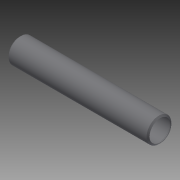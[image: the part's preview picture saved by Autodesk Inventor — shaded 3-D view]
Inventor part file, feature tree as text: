
AUTODESK INVENTOR PART (.ipt)
format: ipt  version: 2014 (Build 180170000, 170)  size: 118,784 bytes
history: native  units: in
note: dims shown in document units (in); Inventor stores cm internally (conversion verified against a paired STEP export)
features: other x56, revolve x1, sketch x1
ambient origin geometry x8: Origin, YZ Plane, XZ Plane, XY Plane, X Axis, Y Axis, Z Axis, Center Point
bodies: Solid1 (feature_tree)
feature tree (58):
  revolve  "Revolution1"  [1 undecoded]
  other  "o1_XY"
  other  "o1_YZ"
  other  "o1_ZX"
  other  "o1_X"
  other  "o1_Y"
  other  "o1_Z"
  other  "o1_Center"
  other  "o2_XY"
  other  "o2_YZ"
  other  "o2_ZX"
  other  "o2_X"
  other  "o2_Y"
  other  "o2_Z"
  other  "o2_Center"
  other  "t1_XY"
  other  "t1_YZ"
  other  "t1_ZX"
  other  "t1_X"
  other  "t1_Y"
  other  "t1_Z"
  other  "t1_Center"
  other  "t2_XY"
  other  "t2_YZ"
  other  "t2_ZX"
  other  "t2_X"
  other  "t2_Y"
  other  "t2_Z"
  other  "t2_Center"
  other  "t3_XY"
  other  "t3_YZ"
  other  "t3_ZX"
  other  "t3_X"
  other  "t3_Y"
  other  "t3_Z"
  other  "t3_Center"
  other  "t4_XY"
  other  "t4_YZ"
  other  "t4_ZX"
  other  "t4_X"
  other  "t4_Y"
  other  "t4_Z"
  other  "t4_Center"
  other  "tube1_XY"
  other  "tube1_YZ"
  other  "tube1_ZX"
  other  "tube1_X"
  other  "tube1_Y"
  other  "tube1_Z"
  other  "tube1_Center"
  other  "tube2_XY"
  other  "tube2_YZ"
  other  "tube2_ZX"
  other  "tube2_X"
  other  "tube2_Y"
  other  "tube2_Z"
  other  "tube2_Center"
  sketch  "Sketch_5"  dims[d0=360.0deg]
note: 1 required parameter value undecoded (feature->parameter linkage not recoverable at this tier; creation-order binding heuristic only, values carry confidence <= 0.55)
